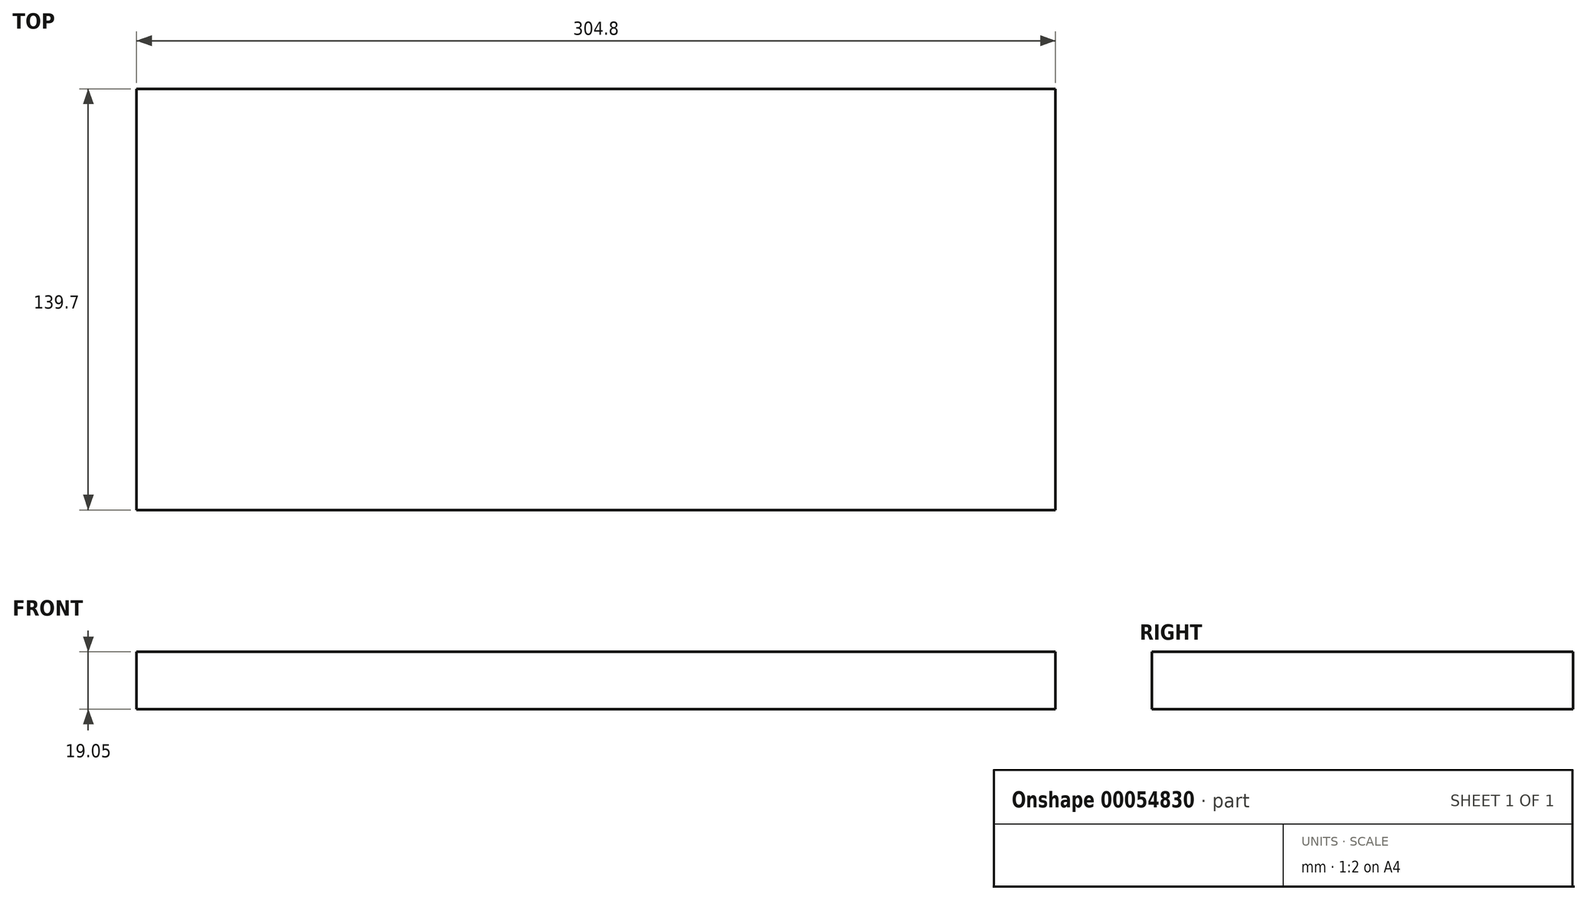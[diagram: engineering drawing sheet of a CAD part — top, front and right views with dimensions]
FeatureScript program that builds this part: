
annotation { "Feature Type Name" : "Feature", "Feature Type Description" : "" }
export const myFeature = defineFeature(function(context is Context, id is Id, definition is map)
    precondition{}
    {
        {
            var Q0;
            Q0=qCreatedBy(makeId("Top.planeOp"),FACE);
            var sketch = newSketch(context, id + "F0", { "sketchPlane" : qUnion([Q0])});
            skLineSegment(sketch, "E0.rect.bottom", {"start": v(-152.4, 69.85) * mm, "end": v(152.4, 69.85) * mm});
            skLineSegment(sketch, "E0.rect.top", {"start": v(-152.4, -69.85) * mm, "end": v(152.4, -69.85) * mm});
            skLineSegment(sketch, "E0.rect.left", {"start": v(-152.4, 69.85) * mm, "end": v(-152.4, -69.85) * mm});
            skLineSegment(sketch, "E0.rect.right", {"start": v(152.4, 69.85) * mm, "end": v(152.4, -69.85) * mm});
            skPoint(sketch, "E0.rect.middle", {"position": v(0, 0) * mm});
            skSolve(sketch);
        }
        {
            var Q0;
            Q0 = qSketchRegion(id + "F0", true);
            extrude(context, id + "F1", {"entities" : qUnion([Q0]), "depth" : 19.05 * mm});
        }
    });
